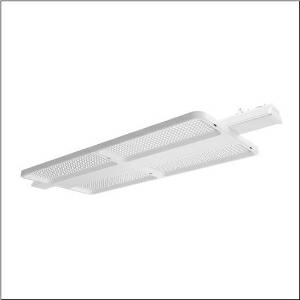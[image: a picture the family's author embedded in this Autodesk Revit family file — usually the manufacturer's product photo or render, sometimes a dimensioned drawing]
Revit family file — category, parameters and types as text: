
# Revit family: highbay_11_fur_licross_r__tragschiene_maxi_51hn12db4vla_45ce
name_source: partatom
category: Lighting Fixtures
units: mm (PartAtom-declared; Revit-internal decimal feet)

## family parameters
Cut with Voids When Loaded = No
Host = Face
Light Source = No
Part Type = Normal
Room Calculation Point = No
Round Connector Dimension = Use Diameter
Shared = No

## types (1)
- --- (1 x LED, 56000 lm, 294.9 W, 4000K)
    Apparent Load = 295 VA
    CIE Flux Codes = 87 98 100 100 100
    Color Rendering = 80
    Color Temperature = 4000K
    Default Elevation = 1800 mm
    Description = high bay luminaire Highbay 11 for Licross® trunking rail maxi; direct symmetric wide distribution, light control with lens of PMMA; UGR ≤ 22 (X = 4H | Y = 8H | S = 0.25H | reflection values 70/50/20); luminous flux: 56.000lm; light colour: 840, colour temperature: 4000K, MacAdam ≤ 2 SDCM (initial), colour rendering: CRI > 80; luminous efficacy: 189,9lm/W; rated service life: 100.000h (L95/B50) at AT= 25°C; control: DALI 2; luminaire connection: plug, 5-pole, with phase selectionmains connection: 230..240V, AC 50/60Hz; connected load: 294,9W; protection rating (complete): IP64; insulation class (complete): insulation class I (protective earthing); protection symbol: D; impact resistance: IK07; certification: CE, ENEC, VDE, UKCA; internal wiring halogen-free; luminaire corresponds to IFS (International Featured Standards) requirements for safety and quality in the food industry; LABS conformity tested according to VDMA 24364:2018-05; housing frame of high-performance plastic PA6, matt traffic white (RAL 9016); cover of PMMA; fixing on rail side of steel, galvanised, white; blank cover of PC/ABS, traffic white (RAL 9016); dimension (LxWxH): 1.250 x 442 x 71mm; permissible operating ambient temperature: -40..+50°C (reducing of maximum allowable ambient temperature of 5°C with ceiling mounting); packaging unit: 1 piece
    Height = 72 mm  [stored 0.23622 ft]
    Lamp = 1 x LED
    Lamp Light Flux = 56000 lm
    Lamp Power = 294.9 W
    Lamp count = 1
    Length = 946 mm
    Luminous efficacy = 190 lm/W
    Manufacturer = Siteco
    ModVariant = No
    Model = 51HN12DB4VLA
    Mounting Place = Ceiling
    Mounting Type = Pendant
    Number of Poles = 1
    OnlyDefault = Yes
    Power Factor = 1
    Product Name = Highbay 11 für Licross® Tragschiene maxi
    Product group = high bay luminaire
    ProductGroupID = 901
    Protection Class = Protection class I
    Protection Degree = IP 64
    RLX_Detail_Level = 1
    RLX_Emergency_Light_Flux = 0 lm
    RLX_Emergency_Type = 0
    RLX_Emergency_Type_DB = No
    RlxData = <blob elided: 24301 chars, md5=d525c934>
    Socket = socket
    Standby Power = 0 W
    System Light Flux = 55999 lm
    System Power = 295 W
    Type Comments = factory setting: luminous flux: 100 % | dim-lin: 254 | 664 mA
    Type Image = l_1361711.jpg
    URL = http://relux.com
    VarID = @adj_025321
    Voltage = 0 V
    Weight = 0.00 kg
    Width = 442 mm

note: [stored X ft] marks values corroborated as IEEE doubles in the binary element streams (Revit-internal decimal feet)

## geometry (parser evidence)
native form markers: Blend x4, Sweep x11
no freeform markers — native parametric forms only
